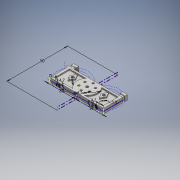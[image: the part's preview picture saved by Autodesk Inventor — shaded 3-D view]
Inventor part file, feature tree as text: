
AUTODESK INVENTOR PART (.ipt)
format: ipt  version: 2016 (Build 200138000, 138)  size: 352,256 bytes
history: native  units: mm
features: extrude x8, other x3, sketch x3, hole x2, fillet x2
ambient origin geometry x8: Origin, YZ Plane, XZ Plane, XY Plane, X Axis, Y Axis, Z Axis, Center Point
bodies: Body1 (feature_tree)
feature tree (18):
  other  "構築線"
  extrude  "押し出し11"  Depth=17.0mm
  extrude  "押し出し12"  Depth=5.6mm
  extrude  "押し出し13"  Depth=10.0mm
  extrude  "押し出し16"  Depth=25.0mm
  other  "固定穴"
  extrude  "押し出し19"  Depth=8.6mm
  extrude  "押し出し20"  TaperAngle=0.0deg  [1 undecoded]
  extrude  "押し出し21"  Depth=20.1mm
  other  "ねじ穴+固定(基板)"
  hole  "ねじ穴(基板)"  [1 undecoded]
  extrude  "押し出し22"  Depth=25.0mm
  fillet  "フィレット1"  Radius=3.0mm
  fillet  "フィレット2"  Radius=20.1mm
  hole  "穴4"  [1 undecoded]
  sketch  "スケッチ8"
  sketch  "スケッチ9"
  sketch  "スケッチ12"
note: 3 required parameter values undecoded (feature->parameter linkage not recoverable at this tier; creation-order binding heuristic only, values carry confidence <= 0.55)
